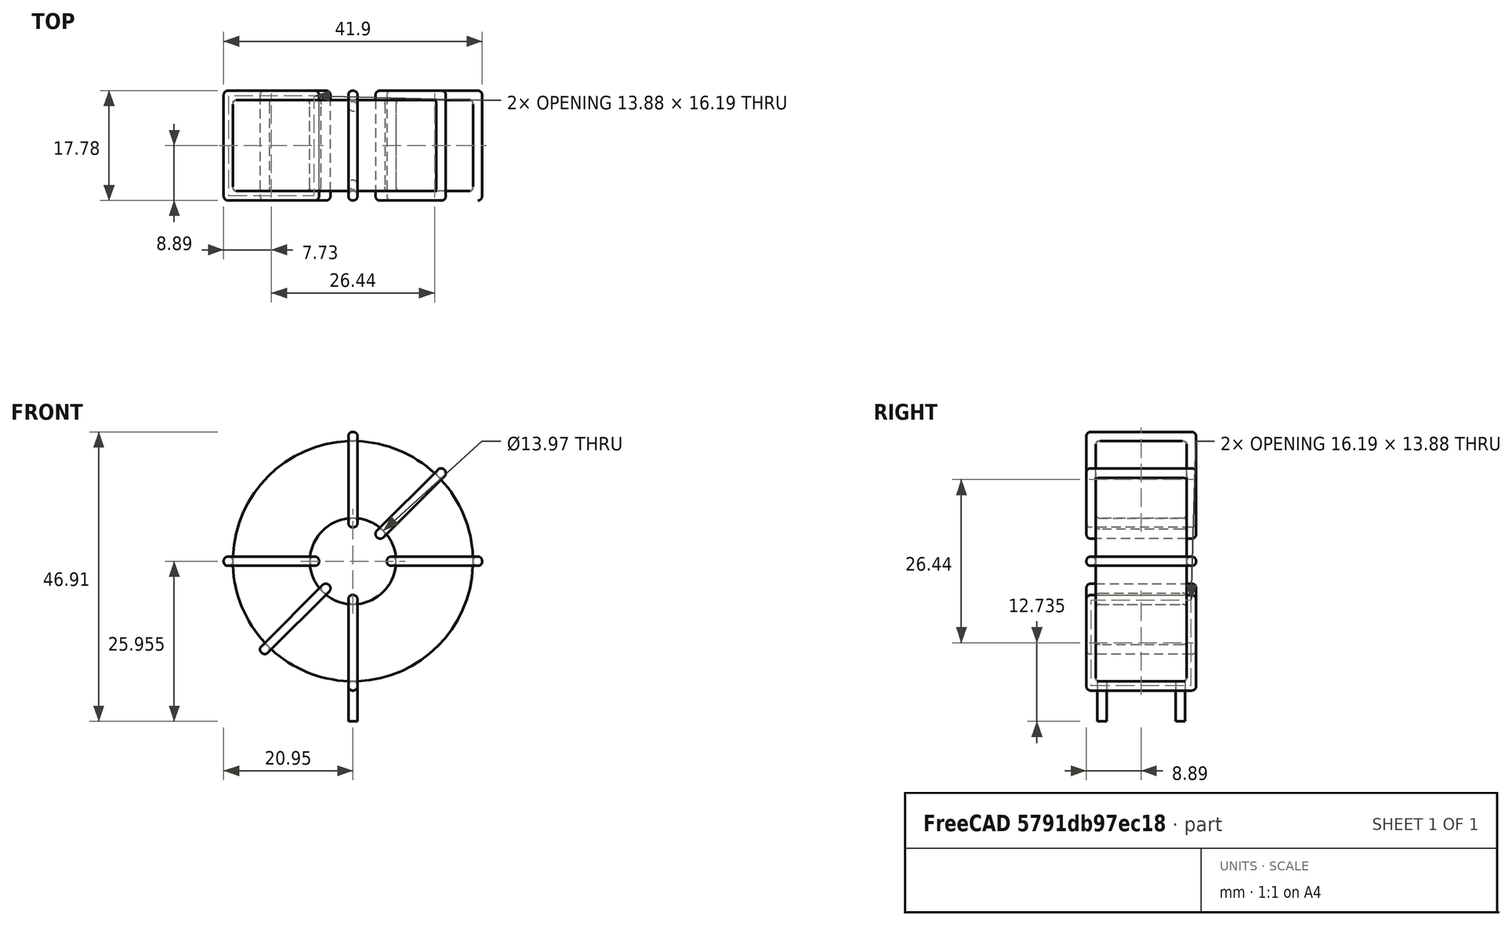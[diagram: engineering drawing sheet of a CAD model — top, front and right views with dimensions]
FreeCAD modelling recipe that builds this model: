
FCSTD DOCUMENT  (FreeCAD 0.16R6703 (Git))
Label: L_Toroid_Vertical_L41.9mm_W17.8mm_P12.70mm_Pulse_F
License: All rights reserved
LicenseURL: http://en.wikipedia.org/wiki/All_rights_reserved
objects: Sketcher::SketchObject×6, PartDesign::Pad×6, PartDesign::Fillet×5, Spreadsheet::Sheet×1
note: 23 computed .brp shape members not serialized (recipe doc carries the construction recipe); baked Part::Feature solids carry a one-line shape summary decoded from their .brp

FEATURE [Spreadsheet::Sheet] Spreadsheet  label="dimensions"
  cells = A1=Wx; B1(Wx)=41.91; C1(WW)=13.97; D1=41.91; A2=Wy; B2(Wy)=17.78; D2=17.78; A3=RM; B3(RMx)=12.7; C3(RMy)=0; A4=d_wire; B4(d_wire)=1.5; A5=H; B5(H)=41.91; A6=offsetx; B6(offsetx)=20.955
FEATURE [Sketcher::SketchObject] Sketch
  Placement = pos=(0,-6.35,0) rot=(1,0,0;1.5708rad)
  expr: Placement.Base.y = -Spreadsheet.RMx / 2
  expr: Constraints[0] = Spreadsheet.Wx / 2 - Spreadsheet.d_wire
  expr: Constraints[4] = Spreadsheet.WW / 2
  expr: Constraints[2] = Spreadsheet.Wx / 2 + Spreadsheet.d_wire + 0.5
  sketch-geometry (2):
    g0: Circle CenterX=0 CenterY=22.955 CenterZ=0 NormalX=0 NormalY=0 NormalZ=1 Radius=19.455
    g1: Circle CenterX=0 CenterY=22.955 CenterZ=0 NormalX=0 NormalY=0 NormalZ=1 Radius=6.985
  constraints (5):
    c: Radius(g0) = 19.455
    c: DistanceX(g-1,g0) = 0
    c: DistanceY(g-1,g0) = 22.955
    c: Coincident(g1,g0)
    c: Radius(g1) = 6.985
FEATURE [PartDesign::Pad] Pad
  Length = 14.78
  Length2 = 100
  Midplane = true
  Placement = pos=(0,-6.35,0) rot=(1,0,0;1.5708rad)
  Sketch = -> Sketch
  Type = 0
  expr: Length = Spreadsheet.Wy - 2 * Spreadsheet.d_wire
FEATURE [Sketcher::SketchObject] Sketch001
  Placement = pos=(0,0,2) rot=(0,0,1;0rad)
  expr: Placement.Base.z = 0.5 + Spreadsheet.d_wire
  expr: Constraints[4] = Spreadsheet.RMy
  expr: Constraints[2] = -Spreadsheet.RMx
  expr: Constraints[1] = Spreadsheet.d_wire / 2
  sketch-geometry (2):
    g0: Circle CenterX=0 CenterY=0 CenterZ=0 NormalX=0 NormalY=0 NormalZ=1 Radius=0.75
    g1: Circle CenterX=0 CenterY=-12.7 CenterZ=0 NormalX=0 NormalY=0 NormalZ=1 Radius=0.75
  constraints (5):
    c: Equal(g0,g1)
    c: Radius(g0) = 0.75
    c: DistanceY(g-1,g1) = -12.7
    c: Coincident(g0,g-1)
    c: DistanceX(g-1,g1) = 0
FEATURE [PartDesign::Pad] Pad001
  Length = 1.5
  Length2 = 5
  Placement = pos=(0,0,2) rot=(0,0,1;0rad)
  Reversed = true
  Sketch = -> Sketch001
  Type = 4
  expr: Length2 = 3.5 + Spreadsheet.d_wire
  expr: Length = Spreadsheet.d_wire
FEATURE [PartDesign::Fillet] Fillet
  Base = -> Pad [Edge6,Edge3,Edge2]
  Placement = pos=(0,-6.35,0) rot=(1,0,0;1.5708rad)
  Radius = 0.5
FEATURE [Sketcher::SketchObject] Sketch003
  Placement = pos=(0,2.54,22.955) rot=(1,0,0;3.14159rad)
  expr: Constraints[18] = Spreadsheet.d_wire
  expr: Constraints[16] = Spreadsheet.d_wire
  expr: Constraints[19] = Spreadsheet.d_wire
  expr: Constraints[17] = Spreadsheet.d_wire
  expr: Placement.Base.y = -1 * (Spreadsheet.RMx - Spreadsheet.Wy) / 2
  expr: Constraints[21] = (Spreadsheet.Wx - Spreadsheet.WW) / 2 - Spreadsheet.d_wire
  expr: Constraints[22] = Spreadsheet.Wx / 2 - Spreadsheet.d_wire
  expr: Constraints[43] = Spreadsheet.d_wire
  expr: Constraints[48] = Spreadsheet.Wx - Spreadsheet.d_wire * 2
  expr: Constraints[49] = Spreadsheet.Wy
  expr: Placement.Base.z = Spreadsheet.Wx / 2 + Spreadsheet.d_wire + 0.5
  sketch-geometry (16):
    g0: LineSegment StartX=-5.485 StartY=0 StartZ=0 EndX=-20.955 EndY=0 EndZ=0
    g1: LineSegment StartX=-20.955 StartY=0 StartZ=0 EndX=-20.955 EndY=17.78 EndZ=0
    g2: LineSegment StartX=-20.955 StartY=17.78 StartZ=0 EndX=-5.485 EndY=17.78 EndZ=0
    g3: LineSegment StartX=-5.485 StartY=17.78 StartZ=0 EndX=-5.485 EndY=0 EndZ=0
    g4: LineSegment StartX=-19.455 StartY=16.28 StartZ=0 EndX=-6.985 EndY=16.28 EndZ=0
    g5: LineSegment StartX=-6.985 StartY=16.28 StartZ=0 EndX=-6.985 EndY=1.5 EndZ=0
    g6: LineSegment StartX=-6.985 StartY=1.5 StartZ=0 EndX=-19.455 EndY=1.5 EndZ=0
    g7: LineSegment StartX=-19.455 StartY=1.5 StartZ=0 EndX=-19.455 EndY=16.28 EndZ=0
    g8: LineSegment StartX=5.485 StartY=17.78 StartZ=0 EndX=20.955 EndY=17.78 EndZ=0
    g9: LineSegment StartX=20.955 StartY=17.78 StartZ=0 EndX=20.955 EndY=0 EndZ=0
    g10: LineSegment StartX=20.955 StartY=0 StartZ=0 EndX=5.485 EndY=0 EndZ=0
    g11: LineSegment StartX=5.485 StartY=0 StartZ=0 EndX=5.485 EndY=17.78 EndZ=0
    g12: LineSegment StartX=6.985 StartY=16.28 StartZ=0 EndX=19.455 EndY=16.28 EndZ=0
    g13: LineSegment StartX=19.455 StartY=16.28 StartZ=0 EndX=19.455 EndY=1.5 EndZ=0
    g14: LineSegment StartX=19.455 StartY=1.5 StartZ=0 EndX=6.985 EndY=1.5 EndZ=0
    g15: LineSegment StartX=6.985 StartY=1.5 StartZ=0 EndX=6.985 EndY=16.28 EndZ=0
  constraints (50):
    c: Horizontal(g0)
    c: Coincident(g1,g0)
    c: Vertical(g1)
    c: Coincident(g2,g1)
    c: Horizontal(g2)
    c: Coincident(g3,g2)
    c: Coincident(g3,g0)
    c: Vertical(g3)
    c: Coincident(g4,g5)
    c: Coincident(g5,g6)
    c: Coincident(g6,g7)
    c: Coincident(g7,g4)
    c: Horizontal(g4)
    c: Horizontal(g6)
    c: Vertical(g5)
    c: Vertical(g7)
    c: DistanceX(g1,g4) = 1.5
    c: DistanceY(g4,g1) = 1.5
    c: DistanceX(g5,g0) = 1.5
    c: DistanceY(g0,g5) = 1.5
    c: DistanceY(g-1,g0) = 0
    c: DistanceX(g6,g6) = 12.47
    c: DistanceX(g6,g-1) = 19.455
    c: Coincident(g8,g9)
    c: Coincident(g9,g10)
    c: Coincident(g10,g11)
    c: Coincident(g11,g8)
    c: Horizontal(g8)
    c: Horizontal(g10)
    c: Vertical(g9)
    c: Vertical(g11)
    c: Coincident(g12,g13)
    c: Coincident(g13,g14)
    c: Coincident(g14,g15)
    c: Coincident(g15,g12)
    c: Horizontal(g12)
    c: Horizontal(g14)
    c: Vertical(g13)
    c: Vertical(g15)
    c: DistanceY(g8,g2) = 0
    c: DistanceY(g10,g0) = 0
    c: DistanceY(g14,g5) = 0
    c: DistanceY(g12,g4) = 0
    c: DistanceX(g8,g12) = 1.5
    c: Equal(g8,g2)
    c: Equal(g12,g4)
    c: Equal(g9,g1)
    c: Equal(g13,g7)
    c: DistanceX(g4,g12) = 38.91
    c: DistanceY(g0,g1) = 17.78
FEATURE [PartDesign::Pad] Pad002
  Length = 1.5
  Length2 = 100
  Midplane = true
  Placement = pos=(0,2.54,22.955) rot=(1,0,0;3.14159rad)
  Sketch = -> Sketch003
  Type = 0
  expr: Length = Spreadsheet.d_wire
FEATURE [PartDesign::Fillet] Fillet001
  Base = -> Pad002 [Edge38,Edge41,Edge42,Edge43,Edge29,Edge32,Edge33,Edge34,Edge25,Edge35,Edge36,Edge13,Edge14,Edge15,Edge16,Edge17,Edge18,Edge19,Edge1,Edge2,Edge3,Edge4,Edge5,Edge6,Edge7,Edge37,Edge39,Edge40,Edge20,Edge23,Edge24,Edge21,Edge22,Edge8,Edge9,Edge10,Edge11,Edge12,Edge26,Edge27,+8 more]
  Placement = pos=(0,2.54,22.955) rot=(1,0,0;3.14159rad)
  Radius = 0.705
  expr: Radius = Spreadsheet.d_wire * 0.47
FEATURE [Sketcher::SketchObject] Sketch004
  Placement = pos=(0,2.54,22.955) rot=(0.92388,0,0.382683;3.14159rad)
  expr: Constraints[18] = Spreadsheet.d_wire
  expr: Constraints[16] = Spreadsheet.d_wire
  expr: Constraints[19] = Spreadsheet.d_wire
  expr: Constraints[17] = Spreadsheet.d_wire
  expr: Placement.Base.y = -1 * (Spreadsheet.RMx - Spreadsheet.Wy) / 2
  expr: Constraints[21] = (Spreadsheet.Wx - Spreadsheet.WW) / 2 - Spreadsheet.d_wire
  expr: Constraints[22] = Spreadsheet.Wx / 2 - Spreadsheet.d_wire
  expr: Constraints[43] = Spreadsheet.d_wire
  expr: Constraints[48] = Spreadsheet.Wx - 2 * Spreadsheet.d_wire
  expr: Constraints[49] = Spreadsheet.Wy
  expr: Placement.Base.z = Spreadsheet.Wx / 2 + Spreadsheet.d_wire + 0.5
  sketch-geometry (16):
    g0: LineSegment StartX=-5.485 StartY=0 StartZ=0 EndX=-20.955 EndY=0 EndZ=0
    g1: LineSegment StartX=-20.955 StartY=0 StartZ=0 EndX=-20.955 EndY=17.78 EndZ=0
    g2: LineSegment StartX=-20.955 StartY=17.78 StartZ=0 EndX=-5.485 EndY=17.78 EndZ=0
    g3: LineSegment StartX=-5.485 StartY=17.78 StartZ=0 EndX=-5.485 EndY=0 EndZ=0
    g4: LineSegment StartX=-19.455 StartY=16.28 StartZ=0 EndX=-6.985 EndY=16.28 EndZ=0
    g5: LineSegment StartX=-6.985 StartY=16.28 StartZ=0 EndX=-6.985 EndY=1.5 EndZ=0
    g6: LineSegment StartX=-6.985 StartY=1.5 StartZ=0 EndX=-19.455 EndY=1.5 EndZ=0
    g7: LineSegment StartX=-19.455 StartY=1.5 StartZ=0 EndX=-19.455 EndY=16.28 EndZ=0
    g8: LineSegment StartX=5.485 StartY=17.78 StartZ=0 EndX=20.955 EndY=17.78 EndZ=0
    g9: LineSegment StartX=20.955 StartY=17.78 StartZ=0 EndX=20.955 EndY=0 EndZ=0
    g10: LineSegment StartX=20.955 StartY=0 StartZ=0 EndX=5.485 EndY=0 EndZ=0
    g11: LineSegment StartX=5.485 StartY=0 StartZ=0 EndX=5.485 EndY=17.78 EndZ=0
    g12: LineSegment StartX=6.985 StartY=16.28 StartZ=0 EndX=19.455 EndY=16.28 EndZ=0
    g13: LineSegment StartX=19.455 StartY=16.28 StartZ=0 EndX=19.455 EndY=1.5 EndZ=0
    g14: LineSegment StartX=19.455 StartY=1.5 StartZ=0 EndX=6.985 EndY=1.5 EndZ=0
    g15: LineSegment StartX=6.985 StartY=1.5 StartZ=0 EndX=6.985 EndY=16.28 EndZ=0
  constraints (50):
    c: Horizontal(g0)
    c: Coincident(g1,g0)
    c: Vertical(g1)
    c: Coincident(g2,g1)
    c: Horizontal(g2)
    c: Coincident(g3,g2)
    c: Coincident(g3,g0)
    c: Vertical(g3)
    c: Coincident(g4,g5)
    c: Coincident(g5,g6)
    c: Coincident(g6,g7)
    c: Coincident(g7,g4)
    c: Horizontal(g4)
    c: Horizontal(g6)
    c: Vertical(g5)
    c: Vertical(g7)
    c: DistanceX(g1,g4) = 1.5
    c: DistanceY(g4,g1) = 1.5
    c: DistanceX(g5,g0) = 1.5
    c: DistanceY(g0,g5) = 1.5
    c: DistanceY(g-1,g0) = 0
    c: DistanceX(g6,g6) = 12.47
    c: DistanceX(g6,g-1) = 19.455
    c: Coincident(g8,g9)
    c: Coincident(g9,g10)
    c: Coincident(g10,g11)
    c: Coincident(g11,g8)
    c: Horizontal(g8)
    c: Horizontal(g10)
    c: Vertical(g9)
    c: Vertical(g11)
    c: Coincident(g12,g13)
    c: Coincident(g13,g14)
    c: Coincident(g14,g15)
    c: Coincident(g15,g12)
    c: Horizontal(g12)
    c: Horizontal(g14)
    c: Vertical(g13)
    c: Vertical(g15)
    c: DistanceY(g8,g2) = 0
    c: DistanceY(g10,g0) = 0
    c: DistanceY(g14,g5) = 0
    c: DistanceY(g12,g4) = 0
    c: DistanceX(g8,g12) = 1.5
    c: Equal(g8,g2)
    c: Equal(g12,g4)
    c: Equal(g9,g1)
    c: Equal(g13,g7)
    c: DistanceX(g4,g12) = 38.91
    c: DistanceY(g0,g1) = 17.78
FEATURE [PartDesign::Pad] Pad003
  Length = 1.5
  Length2 = 100
  Midplane = true
  Placement = pos=(0,2.54,22.955) rot=(0.92388,0,0.382683;3.14159rad)
  Sketch = -> Sketch004
  Type = 0
  expr: Length = Spreadsheet.d_wire
FEATURE [PartDesign::Fillet] Fillet002
  Base = -> Pad003 [Edge38,Edge41,Edge42,Edge43,Edge29,Edge32,Edge33,Edge34,Edge25,Edge35,Edge36,Edge13,Edge14,Edge15,Edge16,Edge17,Edge18,Edge19,Edge1,Edge2,Edge3,Edge4,Edge5,Edge6,Edge7,Edge37,Edge39,Edge40,Edge20,Edge23,Edge24,Edge21,Edge22,Edge8,Edge9,Edge10,Edge11,Edge12,Edge26,Edge27,+8 more]
  Placement = pos=(0,2.54,22.955) rot=(0.92388,0,0.382683;3.14159rad)
  Radius = 0.705
  expr: Radius = Spreadsheet.d_wire * 0.47
FEATURE [Sketcher::SketchObject] Sketch005
  Placement = pos=(0,2.54,22.955) rot=(0.92388,0,-0.382683;3.14159rad)
  expr: Constraints[18] = Spreadsheet.d_wire
  expr: Constraints[16] = Spreadsheet.d_wire
  expr: Constraints[19] = Spreadsheet.d_wire
  expr: Constraints[17] = Spreadsheet.d_wire
  expr: Placement.Base.y = -1 * (Spreadsheet.RMx - Spreadsheet.Wy) / 2
  expr: Constraints[21] = (Spreadsheet.Wx - Spreadsheet.WW) / 2 - Spreadsheet.d_wire
  expr: Constraints[22] = Spreadsheet.Wx / 2 - Spreadsheet.d_wire
  expr: Constraints[43] = Spreadsheet.d_wire
  expr: Constraints[48] = Spreadsheet.Wx - 2 * Spreadsheet.d_wire
  expr: Constraints[49] = Spreadsheet.Wy
  expr: Placement.Base.z = Spreadsheet.Wx / 2 + Spreadsheet.d_wire + 0.5
  sketch-geometry (16):
    g0: LineSegment StartX=-5.485 StartY=0 StartZ=0 EndX=-20.955 EndY=0 EndZ=0
    g1: LineSegment StartX=-20.955 StartY=0 StartZ=0 EndX=-20.955 EndY=17.78 EndZ=0
    g2: LineSegment StartX=-20.955 StartY=17.78 StartZ=0 EndX=-5.485 EndY=17.78 EndZ=0
    g3: LineSegment StartX=-5.485 StartY=17.78 StartZ=0 EndX=-5.485 EndY=0 EndZ=0
    g4: LineSegment StartX=-19.455 StartY=16.28 StartZ=0 EndX=-6.985 EndY=16.28 EndZ=0
    g5: LineSegment StartX=-6.985 StartY=16.28 StartZ=0 EndX=-6.985 EndY=1.5 EndZ=0
    g6: LineSegment StartX=-6.985 StartY=1.5 StartZ=0 EndX=-19.455 EndY=1.5 EndZ=0
    g7: LineSegment StartX=-19.455 StartY=1.5 StartZ=0 EndX=-19.455 EndY=16.28 EndZ=0
    g8: LineSegment StartX=5.485 StartY=17.78 StartZ=0 EndX=20.955 EndY=17.78 EndZ=0
    g9: LineSegment StartX=20.955 StartY=17.78 StartZ=0 EndX=20.955 EndY=0 EndZ=0
    g10: LineSegment StartX=20.955 StartY=0 StartZ=0 EndX=5.485 EndY=0 EndZ=0
    g11: LineSegment StartX=5.485 StartY=0 StartZ=0 EndX=5.485 EndY=17.78 EndZ=0
    g12: LineSegment StartX=6.985 StartY=16.28 StartZ=0 EndX=19.455 EndY=16.28 EndZ=0
    g13: LineSegment StartX=19.455 StartY=16.28 StartZ=0 EndX=19.455 EndY=1.5 EndZ=0
    g14: LineSegment StartX=19.455 StartY=1.5 StartZ=0 EndX=6.985 EndY=1.5 EndZ=0
    g15: LineSegment StartX=6.985 StartY=1.5 StartZ=0 EndX=6.985 EndY=16.28 EndZ=0
  constraints (50):
    c: Horizontal(g0)
    c: Coincident(g1,g0)
    c: Vertical(g1)
    c: Coincident(g2,g1)
    c: Horizontal(g2)
    c: Coincident(g3,g2)
    c: Coincident(g3,g0)
    c: Vertical(g3)
    c: Coincident(g4,g5)
    c: Coincident(g5,g6)
    c: Coincident(g6,g7)
    c: Coincident(g7,g4)
    c: Horizontal(g4)
    c: Horizontal(g6)
    c: Vertical(g5)
    c: Vertical(g7)
    c: DistanceX(g1,g4) = 1.5
    c: DistanceY(g4,g1) = 1.5
    c: DistanceX(g5,g0) = 1.5
    c: DistanceY(g0,g5) = 1.5
    c: DistanceY(g-1,g0) = 0
    c: DistanceX(g6,g6) = 12.47
    c: DistanceX(g6,g-1) = 19.455
    c: Coincident(g8,g9)
    c: Coincident(g9,g10)
    c: Coincident(g10,g11)
    c: Coincident(g11,g8)
    c: Horizontal(g8)
    c: Horizontal(g10)
    c: Vertical(g9)
    c: Vertical(g11)
    c: Coincident(g12,g13)
    c: Coincident(g13,g14)
    c: Coincident(g14,g15)
    c: Coincident(g15,g12)
    c: Horizontal(g12)
    c: Horizontal(g14)
    c: Vertical(g13)
    c: Vertical(g15)
    c: DistanceY(g8,g2) = 0
    c: DistanceY(g10,g0) = 0
    c: DistanceY(g14,g5) = 0
    c: DistanceY(g12,g4) = 0
    c: DistanceX(g8,g12) = 1.5
    c: Equal(g8,g2)
    c: Equal(g12,g4)
    c: Equal(g9,g1)
    c: Equal(g13,g7)
    c: DistanceX(g4,g12) = 38.91
    c: DistanceY(g0,g1) = 17.78
FEATURE [PartDesign::Pad] Pad004
  Length = 1.5
  Length2 = 100
  Midplane = true
  Placement = pos=(0,2.54,22.955) rot=(0.92388,0,-0.382683;3.14159rad)
  Sketch = -> Sketch005
  Type = 0
  expr: Length = Spreadsheet.d_wire
FEATURE [PartDesign::Fillet] Fillet003
  Base = -> Pad004 [Edge38,Edge41,Edge42,Edge43,Edge29,Edge32,Edge33,Edge34,Edge25,Edge35,Edge36,Edge13,Edge14,Edge15,Edge16,Edge17,Edge18,Edge19,Edge1,Edge2,Edge3,Edge4,Edge5,Edge6,Edge7,Edge37,Edge39,Edge40,Edge20,Edge23,Edge24,Edge21,Edge22,Edge8,Edge9,Edge10,Edge11,Edge12,Edge26,Edge27,+8 more]
  Placement = pos=(0,2.54,22.955) rot=(0.92388,0,-0.382683;3.14159rad)
  Radius = 0.705
  expr: Radius = Spreadsheet.d_wire * 0.47
FEATURE [Sketcher::SketchObject] Sketch006
  Placement = pos=(0,2.54,22.955) rot=(0.707107,0,0.707107;3.14159rad)
  expr: Constraints[18] = Spreadsheet.d_wire
  expr: Constraints[16] = Spreadsheet.d_wire
  expr: Constraints[19] = Spreadsheet.d_wire
  expr: Constraints[17] = Spreadsheet.d_wire
  expr: Placement.Base.y = -1 * (Spreadsheet.RMx - Spreadsheet.Wy) / 2
  expr: Constraints[21] = (Spreadsheet.Wx - Spreadsheet.WW) / 2 - Spreadsheet.d_wire
  expr: Constraints[22] = Spreadsheet.Wx / 2 - Spreadsheet.d_wire
  expr: Constraints[43] = Spreadsheet.d_wire
  expr: Constraints[48] = Spreadsheet.Wx - Spreadsheet.d_wire * 2
  expr: Constraints[49] = Spreadsheet.Wy
  expr: Placement.Base.z = Spreadsheet.Wx / 2 + Spreadsheet.d_wire + 0.5
  sketch-geometry (16):
    g0: LineSegment StartX=-5.485 StartY=0 StartZ=0 EndX=-20.955 EndY=0 EndZ=0
    g1: LineSegment StartX=-20.955 StartY=0 StartZ=0 EndX=-20.955 EndY=17.78 EndZ=0
    g2: LineSegment StartX=-20.955 StartY=17.78 StartZ=0 EndX=-5.485 EndY=17.78 EndZ=0
    g3: LineSegment StartX=-5.485 StartY=17.78 StartZ=0 EndX=-5.485 EndY=0 EndZ=0
    g4: LineSegment StartX=-19.455 StartY=16.28 StartZ=0 EndX=-6.985 EndY=16.28 EndZ=0
    g5: LineSegment StartX=-6.985 StartY=16.28 StartZ=0 EndX=-6.985 EndY=1.5 EndZ=0
    g6: LineSegment StartX=-6.985 StartY=1.5 StartZ=0 EndX=-19.455 EndY=1.5 EndZ=0
    g7: LineSegment StartX=-19.455 StartY=1.5 StartZ=0 EndX=-19.455 EndY=16.28 EndZ=0
    g8: LineSegment StartX=5.485 StartY=17.78 StartZ=0 EndX=20.955 EndY=17.78 EndZ=0
    g9: LineSegment StartX=20.955 StartY=17.78 StartZ=0 EndX=20.955 EndY=0 EndZ=0
    g10: LineSegment StartX=20.955 StartY=0 StartZ=0 EndX=5.485 EndY=0 EndZ=0
    g11: LineSegment StartX=5.485 StartY=0 StartZ=0 EndX=5.485 EndY=17.78 EndZ=0
    g12: LineSegment StartX=6.985 StartY=16.28 StartZ=0 EndX=19.455 EndY=16.28 EndZ=0
    g13: LineSegment StartX=19.455 StartY=16.28 StartZ=0 EndX=19.455 EndY=1.5 EndZ=0
    g14: LineSegment StartX=19.455 StartY=1.5 StartZ=0 EndX=6.985 EndY=1.5 EndZ=0
    g15: LineSegment StartX=6.985 StartY=1.5 StartZ=0 EndX=6.985 EndY=16.28 EndZ=0
  constraints (50):
    c: Horizontal(g0)
    c: Coincident(g1,g0)
    c: Vertical(g1)
    c: Coincident(g2,g1)
    c: Horizontal(g2)
    c: Coincident(g3,g2)
    c: Coincident(g3,g0)
    c: Vertical(g3)
    c: Coincident(g4,g5)
    c: Coincident(g5,g6)
    c: Coincident(g6,g7)
    c: Coincident(g7,g4)
    c: Horizontal(g4)
    c: Horizontal(g6)
    c: Vertical(g5)
    c: Vertical(g7)
    c: DistanceX(g1,g4) = 1.5
    c: DistanceY(g4,g1) = 1.5
    c: DistanceX(g5,g0) = 1.5
    c: DistanceY(g0,g5) = 1.5
    c: DistanceY(g-1,g0) = 0
    c: DistanceX(g6,g6) = 12.47
    c: DistanceX(g6,g-1) = 19.455
    c: Coincident(g8,g9)
    c: Coincident(g9,g10)
    c: Coincident(g10,g11)
    c: Coincident(g11,g8)
    c: Horizontal(g8)
    c: Horizontal(g10)
    c: Vertical(g9)
    c: Vertical(g11)
    c: Coincident(g12,g13)
    c: Coincident(g13,g14)
    c: Coincident(g14,g15)
    c: Coincident(g15,g12)
    c: Horizontal(g12)
    c: Horizontal(g14)
    c: Vertical(g13)
    c: Vertical(g15)
    c: DistanceY(g8,g2) = 0
    c: DistanceY(g10,g0) = 0
    c: DistanceY(g14,g5) = 0
    c: DistanceY(g12,g4) = 0
    c: DistanceX(g8,g12) = 1.5
    c: Equal(g8,g2)
    c: Equal(g12,g4)
    c: Equal(g9,g1)
    c: Equal(g13,g7)
    c: DistanceX(g4,g12) = 38.91
    c: DistanceY(g0,g1) = 17.78
FEATURE [PartDesign::Pad] Pad005
  Length = 1.5
  Length2 = 100
  Midplane = true
  Placement = pos=(0,2.54,22.955) rot=(0.707107,0,0.707107;3.14159rad)
  Sketch = -> Sketch006
  Type = 0
  expr: Length = Spreadsheet.d_wire
FEATURE [PartDesign::Fillet] Fillet004
  Base = -> Pad005 [Edge38,Edge41,Edge42,Edge43,Edge29,Edge32,Edge33,Edge34,Edge25,Edge35,Edge36,Edge13,Edge14,Edge15,Edge16,Edge17,Edge18,Edge19,Edge1,Edge2,Edge3,Edge4,Edge5,Edge6,Edge7,Edge37,Edge39,Edge40,Edge20,Edge23,Edge24,Edge21,Edge22,Edge8,Edge9,Edge10,Edge11,Edge12,Edge26,Edge27,+8 more]
  Placement = pos=(0,2.54,22.955) rot=(0.707107,0,0.707107;3.14159rad)
  Radius = 0.705
  expr: Radius = Spreadsheet.d_wire * 0.47
